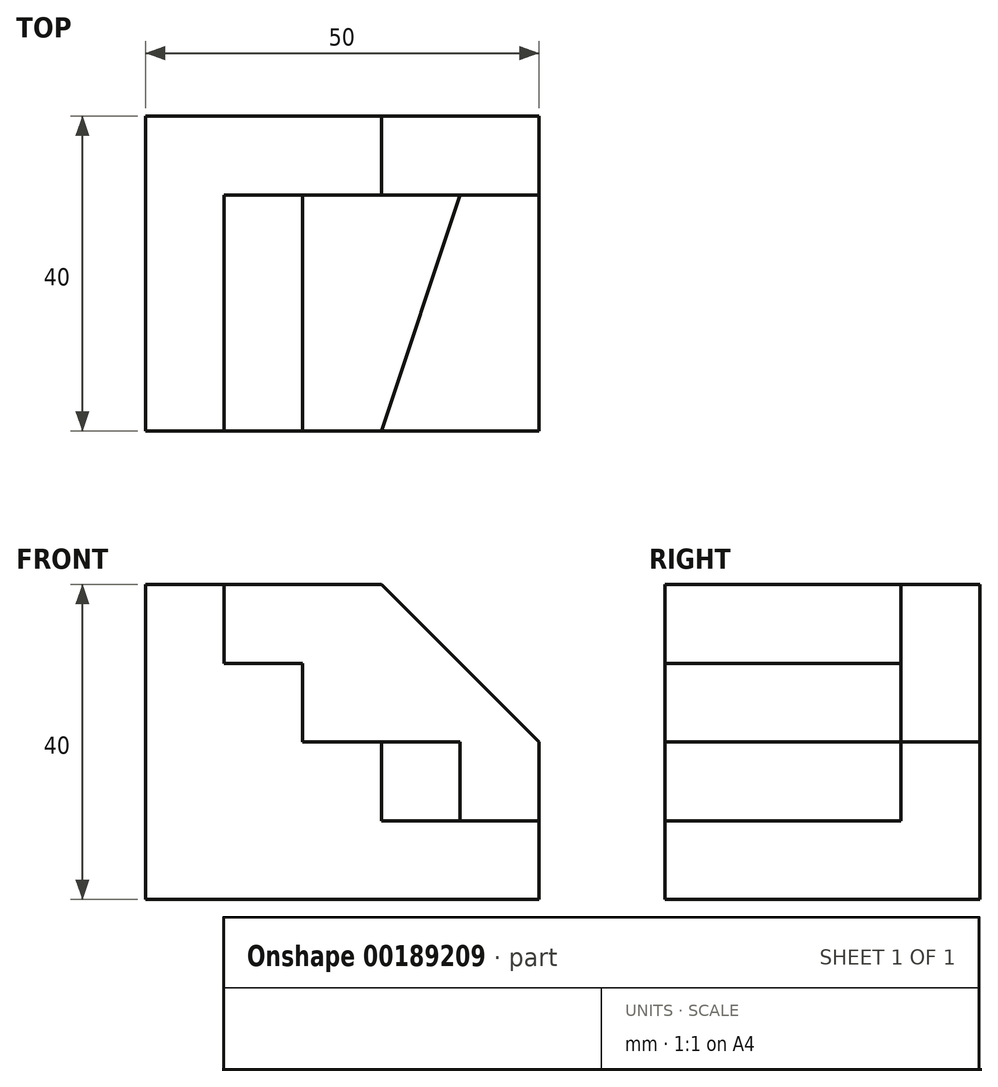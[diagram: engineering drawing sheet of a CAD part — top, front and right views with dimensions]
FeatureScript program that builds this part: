
annotation { "Feature Type Name" : "Feature", "Feature Type Description" : "" }
export const myFeature = defineFeature(function(context is Context, id is Id, definition is map)
    precondition{}
    {
        {
            var Q0;
            Q0=qCreatedBy(makeId("Top.planeOp"),FACE);
            var sketch = newSketch(context, id + "F0", { "sketchPlane" : qUnion([Q0])});
            skLineSegment(sketch, "E0.bottom", {"start": v(0, 0) * mm, "end": v(50, 0) * mm});
            skLineSegment(sketch, "E0.top", {"start": v(0, 40) * mm, "end": v(50, 40) * mm});
            skLineSegment(sketch, "E0.left", {"start": v(0, 0) * mm, "end": v(0, 40) * mm});
            skLineSegment(sketch, "E0.right", {"start": v(50, 0) * mm, "end": v(50, 40) * mm});
            skSolve(sketch);
        }
        {
            var Q0;
            Q0=makeQuery(id+"F0.imprint","IMPRINT",FACE,{"disambiguationData":[TD([[makeQuery(id+"F0.imprint","IMPRINT",EDGE,{"derivedFrom":sQuery(id+"F0.wireOp",EDGE,"E0.bottom")}),1.0]])]});
            extrude(context, id + "F1", {"entities" : qUnion([Q0]), "depth" : 40 * mm});
        }
        {
            var Q0;
            Q0=makeQuery(id+"F1.opExtrude","CAP_FACE",FACE,{"disambiguationData":[OSD([sQuery(id+"F0.wireOp",EDGE,"E0.bottom"),sQuery(id+"F0.wireOp",EDGE,"E0.top"),sQuery(id+"F0.wireOp",EDGE,"E0.left"),sQuery(id+"F0.wireOp",EDGE,"E0.right")])],"isStart":false});
            var sketch = newSketch(context, id + "F2", { "sketchPlane" : qUnion([Q0])});
            skLineSegment(sketch, "E1", {"start": v(50, 30) * mm, "end": v(40, 30) * mm});
            skLineSegment(sketch, "E2", {"start": v(40, 30) * mm, "end": v(30, 0) * mm});
            skLineSegment(sketch, "E3.0", {"start": v(30, 0) * mm, "end": v(50, 0) * mm});
            skLineSegment(sketch, "E4.0", {"start": v(50, 0) * mm, "end": v(50, 30) * mm});
            skPoint(sketch, "E5.orphan", {"position": v(0, 0) * mm});
            skPoint(sketch, "E6.orphan", {"position": v(50, 40) * mm});
            skSolve(sketch);
        }
        {
            var Q0;
            Q0=makeQuery(id+"F2.imprint","IMPRINT",FACE,{"disambiguationData":[TD([[makeQuery(id+"F2.imprint","IMPRINT",EDGE,{"derivedFrom":sQuery(id+"F2.wireOp",EDGE,"E1")}),1.0]])]});
            extrude(context, id + "F3", {"entities" : qUnion([Q0]), "operationType" : NewBodyOperationType.REMOVE, "oppositeDirection" : true, "depth" : 30 * mm});
        }
        {
            var Q0;
            Q0=makeQuery(id+"F1.opExtrude","CAP_FACE",FACE,{"disambiguationData":[OSD([sQuery(id+"F0.wireOp",EDGE,"E0.bottom"),sQuery(id+"F0.wireOp",EDGE,"E0.top"),sQuery(id+"F0.wireOp",EDGE,"E0.left"),sQuery(id+"F0.wireOp",EDGE,"E0.right")])],"isStart":false});
            var sketch = newSketch(context, id + "F4", { "sketchPlane" : qUnion([Q0])});
            skLineSegment(sketch, "E7", {"start": v(40, 30) * mm, "end": v(20, 30) * mm});
            skLineSegment(sketch, "E8", {"start": v(20, 30) * mm, "end": v(20, 0) * mm});
            skLineSegment(sketch, "E9.0", {"start": v(20, 0) * mm, "end": v(30, 0) * mm});
            skLineSegment(sketch, "E10.0", {"start": v(40, 30) * mm, "end": v(30, 0) * mm});
            skPoint(sketch, "E11.orphan", {"position": v(0, 0) * mm});
            skSolve(sketch);
        }
        {
            var Q0;
            Q0=makeQuery(id+"F4.imprint","IMPRINT",FACE,{"disambiguationData":[TD([[makeQuery(id+"F4.imprint","IMPRINT",EDGE,{"derivedFrom":sQuery(id+"F4.wireOp",EDGE,"E7")}),1.0]])]});
            extrude(context, id + "F5", {"entities" : qUnion([Q0]), "operationType" : NewBodyOperationType.REMOVE, "oppositeDirection" : true, "depth" : 20 * mm});
        }
        {
            var Q0;
            Q0=makeQuery(id+"F1.opExtrude","CAP_FACE",FACE,{"disambiguationData":[OSD([sQuery(id+"F0.wireOp",EDGE,"E0.bottom"),sQuery(id+"F0.wireOp",EDGE,"E0.top"),sQuery(id+"F0.wireOp",EDGE,"E0.left"),sQuery(id+"F0.wireOp",EDGE,"E0.right")])],"isStart":false});
            var sketch = newSketch(context, id + "F6", { "sketchPlane" : qUnion([Q0])});
            skLineSegment(sketch, "E12.bottom", {"start": v(20, 30) * mm, "end": v(10, 30) * mm});
            skLineSegment(sketch, "E12.top", {"start": v(20, 0) * mm, "end": v(10, 0) * mm});
            skLineSegment(sketch, "E12.left", {"start": v(20, 30) * mm, "end": v(20, 0) * mm});
            skLineSegment(sketch, "E12.right", {"start": v(10, 30) * mm, "end": v(10, 0) * mm});
            skSolve(sketch);
        }
        {
            var Q0;
            Q0=makeQuery(id+"F6.imprint","IMPRINT",FACE,{"disambiguationData":[TD([[makeQuery(id+"F6.imprint","IMPRINT",EDGE,{"derivedFrom":sQuery(id+"F6.wireOp",EDGE,"E12.bottom")}),1.0]])]});
            extrude(context, id + "F7", {"entities" : qUnion([Q0]), "operationType" : NewBodyOperationType.REMOVE, "oppositeDirection" : true, "depth" : 10 * mm});
        }
        {
            var Q0;
            Q0=makeQuery(id+"F1.opExtrude","CAP_EDGE",EDGE,{"disambiguationData":[OSD([sQuery(id+"F0.wireOp",EDGE,"E0.right")])],"isStart":false});
            chamfer(context, id + "F8", {"entities" : qUnion([Q0]), "width" : 20 * mm, "tangentPropagation" : true});
        }
    });
